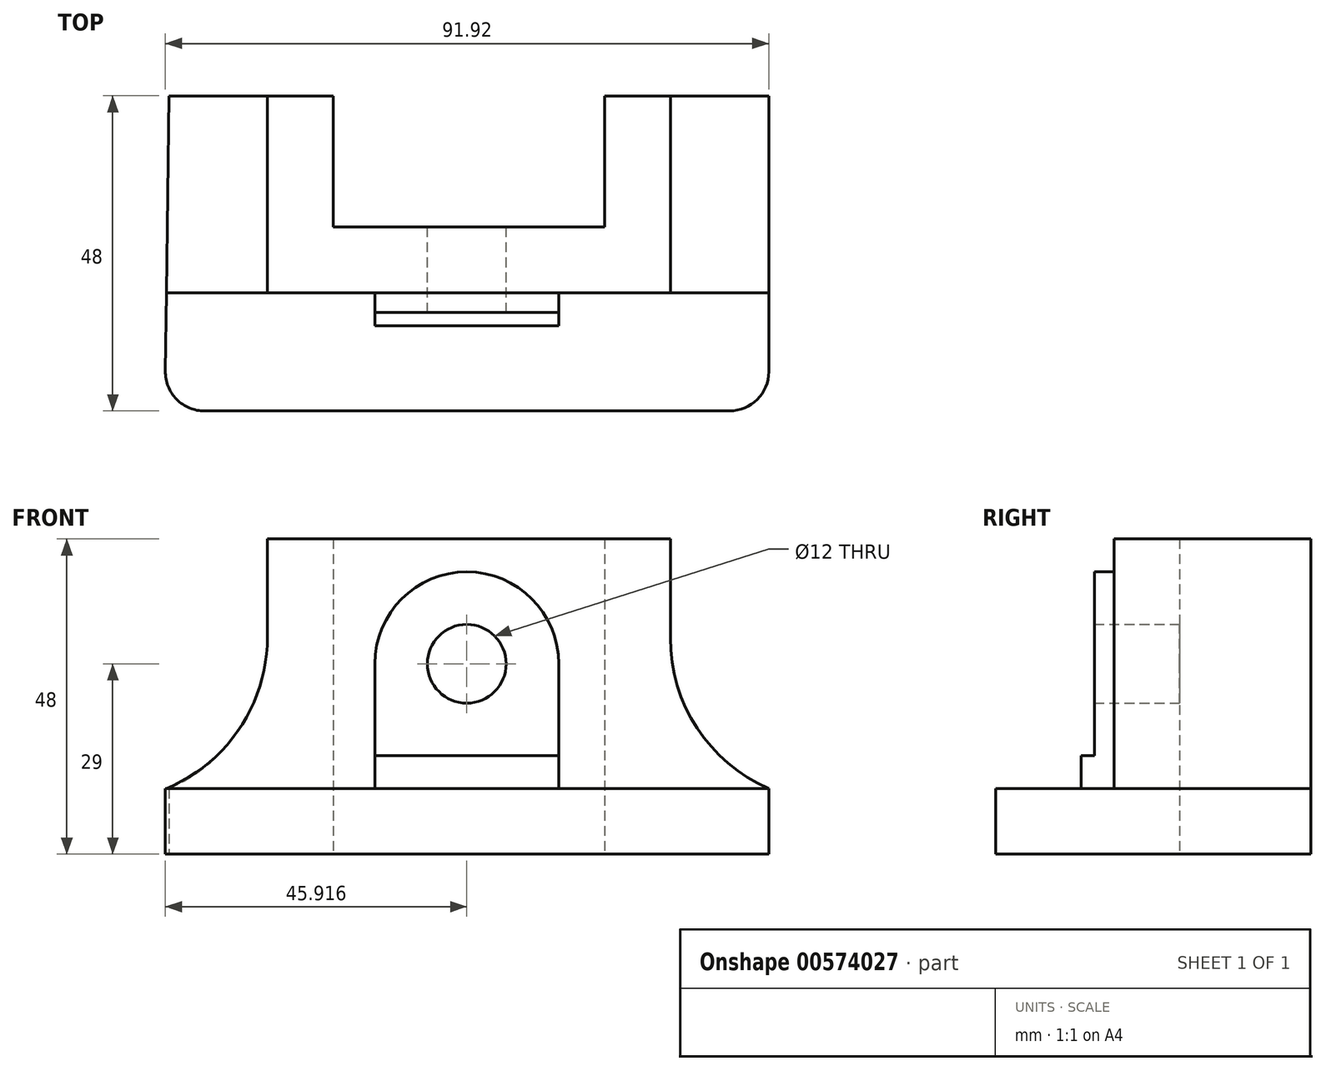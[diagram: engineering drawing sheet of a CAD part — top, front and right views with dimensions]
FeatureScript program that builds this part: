
annotation { "Feature Type Name" : "Feature", "Feature Type Description" : "" }
export const myFeature = defineFeature(function(context is Context, id is Id, definition is map)
    precondition{}
    {
        {
            var Q0;
            Q0=qCreatedBy(makeId("Top.planeOp"),FACE);
            var sketch = newSketch(context, id + "F0", { "sketchPlane" : qUnion([Q0])});
            skLineSegment(sketch, "E0", {"start": v(-52.98, 33.44) * mm, "end": v(-37.98, 33.44) * mm});
            skLineSegment(sketch, "E1", {"start": v(-37.98, 33.44) * mm, "end": v(-37.98, 3.44) * mm});
            skLineSegment(sketch, "E2", {"start": v(-37.98, 3.44) * mm, "end": v(23.39, 3.44) * mm});
            skLineSegment(sketch, "E3", {"start": v(23.39, 3.44) * mm, "end": v(23.39, 33.44) * mm});
            skLineSegment(sketch, "E4", {"start": v(23.39, 33.44) * mm, "end": v(38.39, 33.44) * mm});
            skLineSegment(sketch, "E5", {"start": v(38.39, 33.44) * mm, "end": v(38.39, -8.56) * mm});
            skLineSegment(sketch, "E6", {"start": v(32.39, -14.56) * mm, "end": v(-47.53, -14.56) * mm});
            skLineSegment(sketch, "E7", {"start": v(-53.53, -8.48) * mm, "end": v(-52.98, 33.44) * mm});
            skLineSegment(sketch, "E8", {"start": v(-37.98, 33.44) * mm, "end": v(-27.98, 33.44) * mm});
            skLineSegment(sketch, "E9", {"start": v(-27.98, 33.44) * mm, "end": v(-27.98, 13.44) * mm});
            skLineSegment(sketch, "E10", {"start": v(-27.98, 13.44) * mm, "end": v(13.39, 13.44) * mm});
            skLineSegment(sketch, "E11", {"start": v(13.39, 13.44) * mm, "end": v(13.39, 33.44) * mm});
            skLineSegment(sketch, "E12", {"start": v(13.39, 33.44) * mm, "end": v(23.39, 33.44) * mm});
            skPoint(sketch, "E13.visualSharp", {"position": v(38.39, -14.56) * mm});
            skArc(sketch, "E13.filletArc", {"start": v(32.39, -14.56) * mm, "mid": v(36.63, -12.8) * mm, "end": v(38.39, -8.56) * mm});
            skPoint(sketch, "E14.visualSharp", {"position": v(-53.61, -14.56) * mm});
            skArc(sketch, "E14.filletArc", {"start": v(-53.53, -8.48) * mm, "mid": v(-51.8, -12.78) * mm, "end": v(-47.53, -14.56) * mm});
            skSolve(sketch);
        }
        {
            var Q0;
            Q0=makeQuery(id+"F0.imprint","IMPRINT",FACE,{"disambiguationData":[TD([[makeQuery(id+"F0.imprint","IMPRINT",EDGE,{"derivedFrom":sQuery(id+"F0.wireOp",EDGE,"E1")}),1.0]])]});
            extrude(context, id + "F1", {"entities" : qUnion([Q0]), "depth" : 48 * mm, "offsetDistance" : 25 * mm});
        }
        {
            var Q0;
            Q0 = qSketchRegion(id + "F0", true);
            extrude(context, id + "F2", {"entities" : qUnion([Q0]), "operationType" : NewBodyOperationType.ADD, "depth" : 10 * mm, "offsetDistance" : 25 * mm});
        }
        {
            var Q0;
            Q0=makeQuery(id+"F1.opExtrude","SWEPT_FACE",FACE,{"disambiguationData":[OSD([sQuery(id+"F0.wireOp",EDGE,"E2")])]});
            var sketch = newSketch(context, id + "F3", { "sketchPlane" : qUnion([Q0])});
            skCircle(sketch, "E15", {"center": v(-7.61, 29) * mm, "radius": 6 * mm});
            skArc(sketch, "E16", {"start": v(6.39, 29) * mm, "mid": v(-7.61, 43) * mm, "end": v(-21.61, 29) * mm});
            skLineSegment(sketch, "E17", {"start": v(-21.61, 29) * mm, "end": v(-21.61, 10) * mm});
            skLineSegment(sketch, "E18", {"start": v(6.39, 29) * mm, "end": v(6.39, 10) * mm});
            skLineSegment(sketch, "E19.bottom", {"start": v(-21.61, 15) * mm, "end": v(6.39, 15) * mm});
            skLineSegment(sketch, "E19.top", {"start": v(-21.61, 10) * mm, "end": v(6.39, 10) * mm});
            skLineSegment(sketch, "E19.left", {"start": v(-21.61, 15) * mm, "end": v(-21.61, 10) * mm});
            skLineSegment(sketch, "E19.right", {"start": v(6.39, 15) * mm, "end": v(6.39, 10) * mm});
            skSolve(sketch);
        }
        {
            var Q0;
            Q0=makeQuery(id+"F3.imprint","IMPRINT",FACE,{"disambiguationData":[TD([[makeQuery(id+"F3.imprint","IMPRINT",EDGE,{"derivedFrom":sQuery(id+"F3.wireOp",EDGE,"E15")}),-1.0]])]});
            extrude(context, id + "F4", {"entities" : qUnion([Q0]), "operationType" : NewBodyOperationType.ADD, "depth" : 3 * mm, "offsetDistance" : 25 * mm});
        }
        {
            var Q0;
            Q0=makeQuery(id+"F3.imprint","IMPRINT",FACE,{"disambiguationData":[TD([[makeQuery(id+"F3.imprint","IMPRINT",EDGE,{"derivedFrom":sQuery(id+"F3.wireOp",EDGE,"E19.bottom")}),-1.0]])]});
            extrude(context, id + "F5", {"entities" : qUnion([Q0]), "operationType" : NewBodyOperationType.ADD, "depth" : 5 * mm, "offsetDistance" : 25 * mm});
        }
        {
            var Q0;
            Q0=sQuery(id+"F3.wireOp",VERTEX,"E15.center");
            var Q1;
            Q1=makeQuery(id+"F1.opExtrude","SWEPT_BODY",BODY,{"disambiguationData":[OSD([sQuery(id+"F0.wireOp",EDGE,"E1"),sQuery(id+"F0.wireOp",EDGE,"E2"),sQuery(id+"F0.wireOp",EDGE,"E3"),sQuery(id+"F0.wireOp",EDGE,"E8"),sQuery(id+"F0.wireOp",EDGE,"E9"),sQuery(id+"F0.wireOp",EDGE,"E10"),sQuery(id+"F0.wireOp",EDGE,"E11"),sQuery(id+"F0.wireOp",EDGE,"E12")])]});
            hole(context, id + "F6", {"style" : HoleStyle.SIMPLE, "endStyle" : HoleEndStyle.THROUGH, "holeDiameter" : 12 * mm, "isTappedThrough" : true, "tappedDepth" : 12 * mm, "tapClearance" : 3, "locations" : qUnion([Q0]), "scope" : qUnion([Q1])});
        }
        {
            var Q0;
            Q0=makeQuery(id+"F2.boolean.opBoolean","INTERSECT",EDGE,{"derivedFrom":[makeQuery(id+"F1.opExtrude","SWEPT_FACE",FACE,{"disambiguationData":[OSD([sQuery(id+"F0.wireOp",EDGE,"E1")])]}),makeQuery(id+"F2.opExtrude","CAP_FACE",FACE,{"disambiguationData":[OSD([sQuery(id+"F0.wireOp",EDGE,"E0"),sQuery(id+"F0.wireOp",EDGE,"E4"),sQuery(id+"F0.wireOp",EDGE,"E5"),sQuery(id+"F0.wireOp",EDGE,"E6"),sQuery(id+"F0.wireOp",EDGE,"E7"),sQuery(id+"F0.wireOp",EDGE,"E8"),sQuery(id+"F0.wireOp",EDGE,"E9"),sQuery(id+"F0.wireOp",EDGE,"E10"),sQuery(id+"F0.wireOp",EDGE,"E11"),sQuery(id+"F0.wireOp",EDGE,"E12"),sQuery(id+"F0.wireOp",EDGE,"E13.filletArc"),sQuery(id+"F0.wireOp",EDGE,"E14.filletArc")])],"isStart":false})]});
            fillet(context, id + "F7", {"entities" : qUnion([Q0]), "radius" : 25 * mm, "tangentPropagation" : true, "allowEdgeOverflow" : false});
        }
        {
            var Q0;
            Q0=makeQuery(id+"F2.boolean.opBoolean","INTERSECT",EDGE,{"derivedFrom":[makeQuery(id+"F1.opExtrude","SWEPT_FACE",FACE,{"disambiguationData":[OSD([sQuery(id+"F0.wireOp",EDGE,"E3")])]}),makeQuery(id+"F2.opExtrude","CAP_FACE",FACE,{"disambiguationData":[OSD([sQuery(id+"F0.wireOp",EDGE,"E0"),sQuery(id+"F0.wireOp",EDGE,"E4"),sQuery(id+"F0.wireOp",EDGE,"E5"),sQuery(id+"F0.wireOp",EDGE,"E6"),sQuery(id+"F0.wireOp",EDGE,"E7"),sQuery(id+"F0.wireOp",EDGE,"E8"),sQuery(id+"F0.wireOp",EDGE,"E9"),sQuery(id+"F0.wireOp",EDGE,"E10"),sQuery(id+"F0.wireOp",EDGE,"E11"),sQuery(id+"F0.wireOp",EDGE,"E12"),sQuery(id+"F0.wireOp",EDGE,"E13.filletArc"),sQuery(id+"F0.wireOp",EDGE,"E14.filletArc")])],"isStart":false})]});
            fillet(context, id + "F8", {"entities" : qUnion([Q0]), "radius" : 25 * mm, "tangentPropagation" : true, "allowEdgeOverflow" : false});
        }
    });
